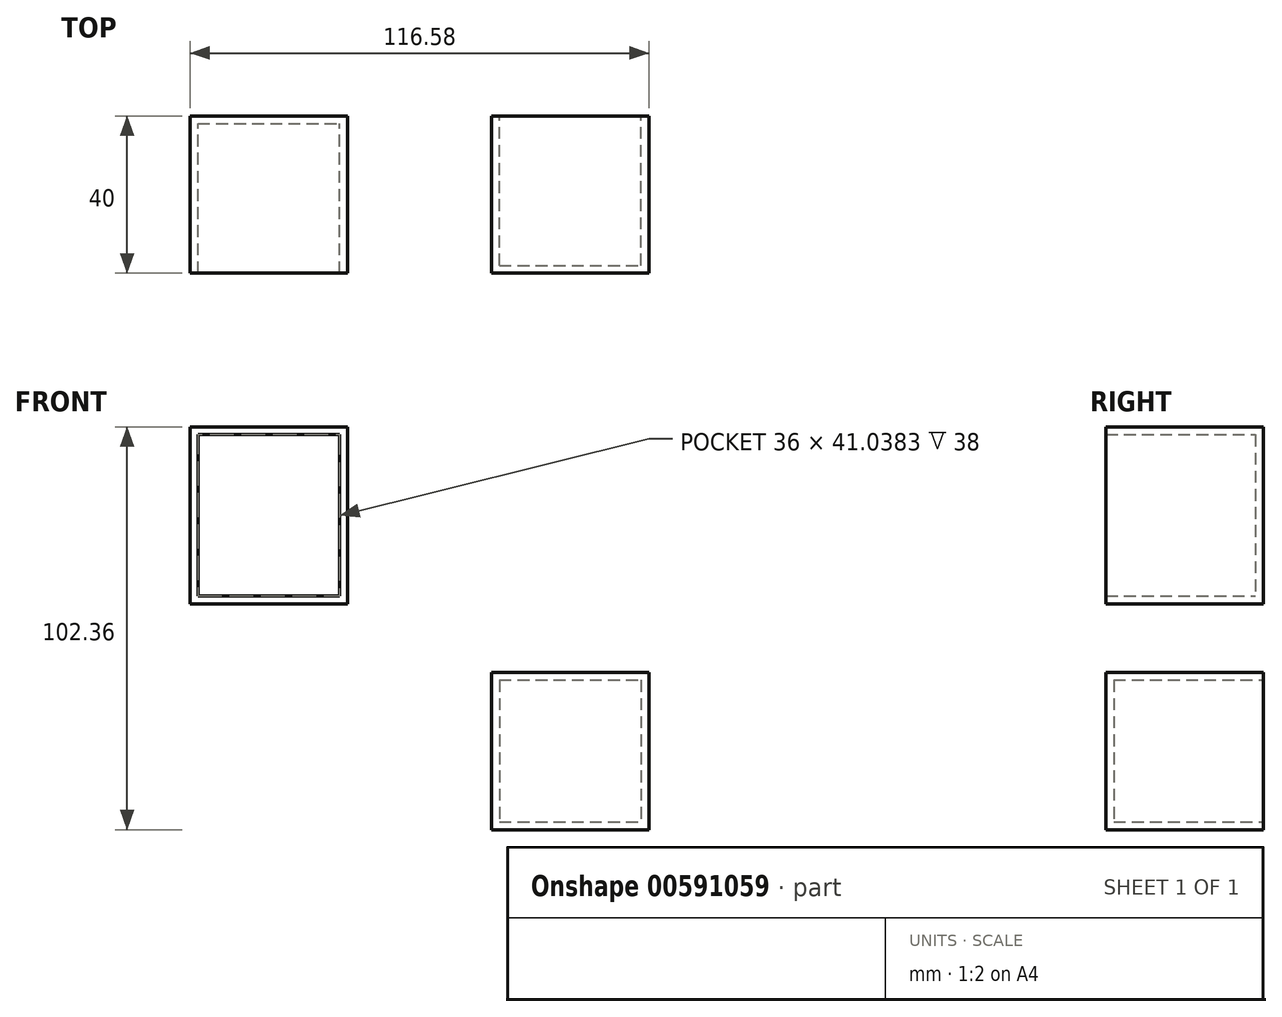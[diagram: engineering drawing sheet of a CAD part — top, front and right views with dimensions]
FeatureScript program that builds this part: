
annotation { "Feature Type Name" : "Feature", "Feature Type Description" : "" }
export const myFeature = defineFeature(function(context is Context, id is Id, definition is map)
    precondition{}
    {
        {
            var Q0;
            Q0=qCreatedBy(makeId("Front.planeOp"),FACE);
            var sketch = newSketch(context, id + "F0", { "sketchPlane" : qUnion([Q0])});
            skLineSegment(sketch, "E0.bottom", {"start": v(-76.58, 62.36) * mm, "end": v(-36.58, 62.36) * mm});
            skLineSegment(sketch, "E0.top", {"start": v(-76.58, 17.32) * mm, "end": v(-36.58, 17.32) * mm});
            skLineSegment(sketch, "E0.left", {"start": v(-76.58, 62.36) * mm, "end": v(-76.58, 17.32) * mm});
            skLineSegment(sketch, "E0.right", {"start": v(-36.58, 62.36) * mm, "end": v(-36.58, 17.32) * mm});
            skLineSegment(sketch, "E1.bottom", {"start": v(-51.94, 77.86) * mm, "end": v(-53.63, 77.86) * mm});
            skLineSegment(sketch, "E1.top", {"start": v(-51.94, 84.62) * mm, "end": v(-53.63, 84.62) * mm});
            skLineSegment(sketch, "E1.left", {"start": v(-51.94, 77.86) * mm, "end": v(-51.94, 84.62) * mm});
            skLineSegment(sketch, "E1.right", {"start": v(-53.63, 77.86) * mm, "end": v(-53.63, 84.62) * mm});
            skSolve(sketch);
        }
        {
            var Q0;
            Q0=makeQuery(id+"F0.imprint","IMPRINT",FACE,{"disambiguationData":[TD([[makeQuery(id+"F0.imprint","IMPRINT",EDGE,{"derivedFrom":sQuery(id+"F0.wireOp",EDGE,"E0.bottom")}),-1.0]])]});
            extrude(context, id + "F1", {"entities" : qUnion([Q0]), "depth" : 40 * mm, "offsetDistance" : 25 * mm});
        }
        {
            var Q0;
            Q0=makeQuery(id+"F1.opExtrude","CAP_FACE",FACE,{"disambiguationData":[OSD([sQuery(id+"F0.wireOp",EDGE,"E0.bottom"),sQuery(id+"F0.wireOp",EDGE,"E0.top"),sQuery(id+"F0.wireOp",EDGE,"E0.left"),sQuery(id+"F0.wireOp",EDGE,"E0.right")])],"isStart":false});
            shell(context, id + "F2", {"entities" : qUnion([Q0]), "thickness" : 2 * mm});
        }
        {
            var Q0;
            Q0=makeQuery(id+"F1.opExtrude","CAP_FACE",FACE,{"disambiguationData":[OSD([sQuery(id+"F0.wireOp",EDGE,"E0.bottom"),sQuery(id+"F0.wireOp",EDGE,"E0.top"),sQuery(id+"F0.wireOp",EDGE,"E0.left"),sQuery(id+"F0.wireOp",EDGE,"E0.right")])],"isStart":false});
            var sketch = newSketch(context, id + "F3", { "sketchPlane" : qUnion([Q0])});
            skSolve(sketch);
        }
        {
            var Q0;
            Q0=qCreatedBy(makeId("Front.planeOp"),FACE);
            var sketch = newSketch(context, id + "F4", { "sketchPlane" : qUnion([Q0])});
            skLineSegment(sketch, "E2.bottom", {"start": v(0, 0) * mm, "end": v(40, 0) * mm});
            skLineSegment(sketch, "E2.top", {"start": v(0, -40) * mm, "end": v(40, -40) * mm});
            skLineSegment(sketch, "E2.left", {"start": v(0, 0) * mm, "end": v(0, -40) * mm});
            skLineSegment(sketch, "E2.right", {"start": v(40, 0) * mm, "end": v(40, -40) * mm});
            skSolve(sketch);
        }
        {
            var Q0;
            Q0=makeQuery(id+"F4.imprint","IMPRINT",FACE,{"disambiguationData":[TD([[makeQuery(id+"F4.imprint","IMPRINT",EDGE,{"derivedFrom":sQuery(id+"F4.wireOp",EDGE,"E2.bottom")}),-1.0]])]});
            extrude(context, id + "F5", {"entities" : qUnion([Q0]), "depth" : 40 * mm, "offsetDistance" : 25 * mm});
        }
        {
            var Q0;
            Q0=makeQuery(id+"F5.opExtrude","CAP_FACE",FACE,{"disambiguationData":[OSD([sQuery(id+"F4.wireOp",EDGE,"E2.bottom"),sQuery(id+"F4.wireOp",EDGE,"E2.top"),sQuery(id+"F4.wireOp",EDGE,"E2.left"),sQuery(id+"F4.wireOp",EDGE,"E2.right")])],"isStart":true});
            shell(context, id + "F6", {"entities" : qUnion([Q0]), "thickness" : 2 * mm});
        }
    });
